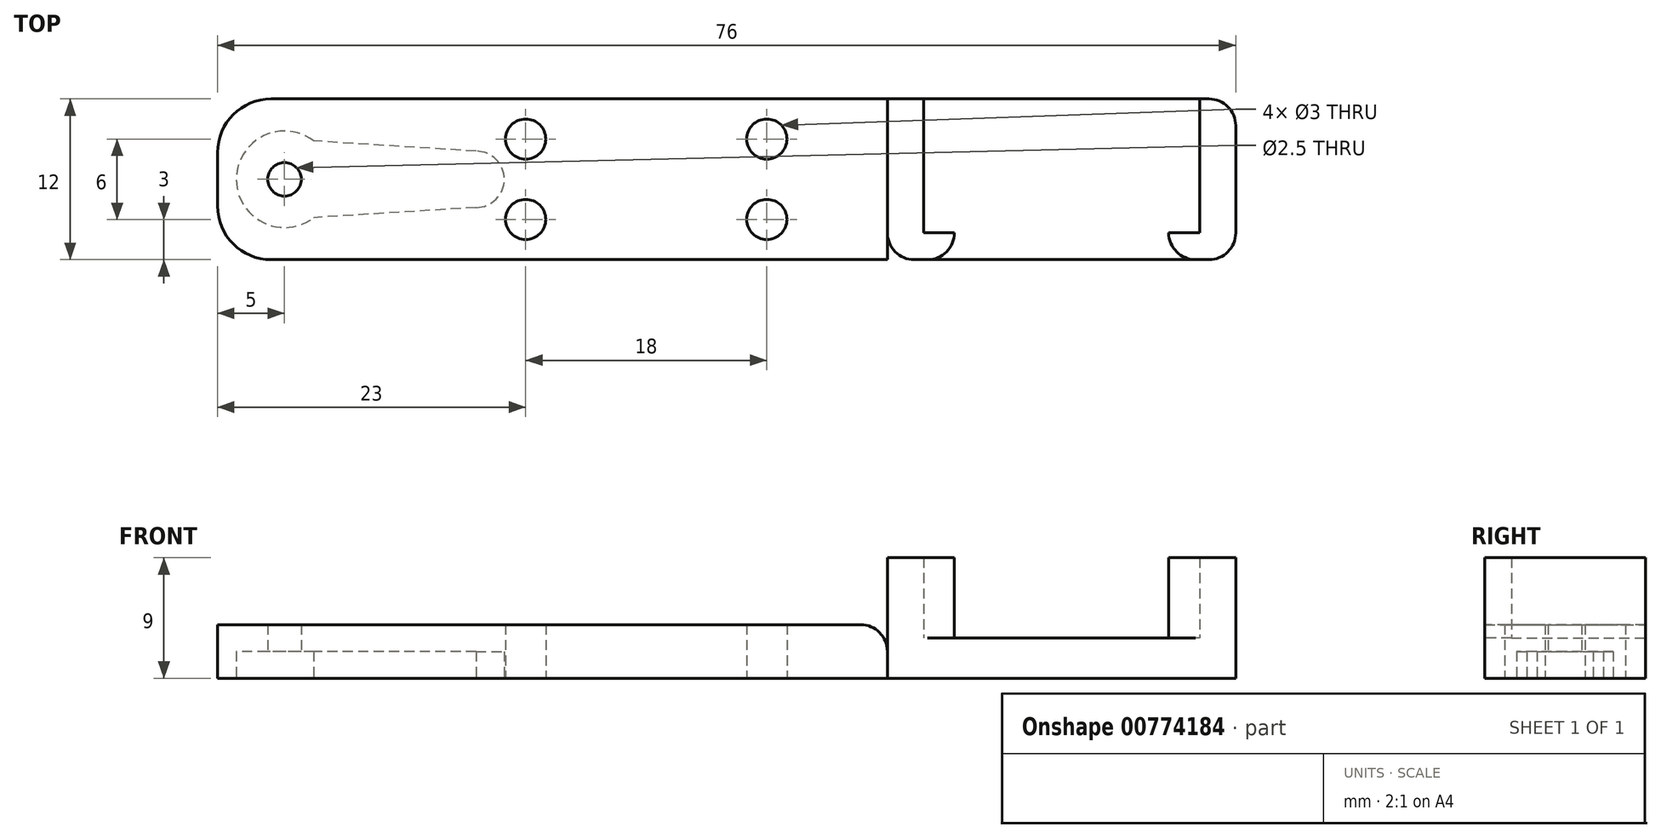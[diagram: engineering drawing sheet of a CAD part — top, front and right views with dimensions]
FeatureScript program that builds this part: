
annotation { "Feature Type Name" : "Feature", "Feature Type Description" : "" }
export const myFeature = defineFeature(function(context is Context, id is Id, definition is map)
    precondition{}
    {
        {
            var Q0;
            Q0=qCreatedBy(makeId("Top.planeOp"),FACE);
            var sketch = newSketch(context, id + "F0", { "sketchPlane" : qUnion([Q0])});
            skCircle(sketch, "E0", {"center": v(0, 0) * mm, "radius": 3.6 * mm});
            skLineSegment(sketch, "E1", {"start": v(0, 0) * mm, "end": v(0, 3) * mm});
            skLineSegment(sketch, "E2", {"start": v(0, 0) * mm, "end": v(0, -3) * mm, "construction": true});
            skLineSegment(sketch, "E3", {"start": v(0, 0) * mm, "end": v(14.3, 0) * mm});
            skLineSegment(sketch, "E4", {"start": v(14.3, 0) * mm, "end": v(14.3, -2.1) * mm});
            skArc(sketch, "E5", {"start": v(14.3, -2.1) * mm, "mid": v(16.4, 0) * mm, "end": v(14.3, 2.1) * mm});
            skLineSegment(sketch, "E6", {"start": v(14.3, 2.1) * mm, "end": v(0, 3) * mm});
            skLineSegment(sketch, "E7", {"start": v(14.3, -2.1) * mm, "end": v(0, -3) * mm});
            skSolve(sketch);
        }
        {
            var Q0;
            Q0 = qSketchRegion(id + "F0", true);
            extrude(context, id + "F1", {"entities" : qUnion([Q0]), "depth" : 2 * mm, "offsetDistance" : 25 * mm});
        }
        {
            var Q0;
            Q0=qCreatedBy(makeId("Top.planeOp"),FACE);
            var sketch = newSketch(context, id + "F2", { "sketchPlane" : qUnion([Q0])});
            skLineSegment(sketch, "E8.bottom", {"start": v(25, -6) * mm, "end": v(-25, -6) * mm});
            skLineSegment(sketch, "E8.top", {"start": v(25, 6) * mm, "end": v(-25, 6) * mm});
            skLineSegment(sketch, "E8.left", {"start": v(25, -6) * mm, "end": v(25, 6) * mm});
            skLineSegment(sketch, "E8.right", {"start": v(-25, -6) * mm, "end": v(-25, 6) * mm});
            skPoint(sketch, "E8.middle", {"position": v(0, 0) * mm});
            skSolve(sketch);
        }
        {
            var Q0;
            Q0 = qSketchRegion(id + "F2", true);
            extrude(context, id + "F3", {"entities" : qUnion([Q0]), "depth" : 4 * mm, "offsetDistance" : 25 * mm});
        }
        {
            var Q0;
            Q0=makeQuery(id+"F3.opExtrude","SWEPT_BODY",BODY,{"disambiguationData":[OSD([sQuery(id+"F2.wireOp",EDGE,"E8.bottom"),sQuery(id+"F2.wireOp",EDGE,"E8.top"),sQuery(id+"F2.wireOp",EDGE,"E8.left"),sQuery(id+"F2.wireOp",EDGE,"E8.right")])]});
            transform(context, id + "F4", {"entities" : qUnion([Q0]), "transformType" : TransformType.TRANSLATION_3D, "dx" : 20 * mm, "dy" : 0 * mm, "dz" : 0 * mm, "makeCopy" : false});
        }
        {
            var Q0;
            Q0=makeQuery(id+"F1.opExtrude","SWEPT_BODY",BODY,{"disambiguationData":[OSD([sQuery(id+"F0.wireOp",EDGE,"E0"),sQuery(id+"F0.wireOp",EDGE,"GIS3N8ls-1sfF-PQuO-XVTb-pW0GfDq8woWl"),sQuery(id+"F0.wireOp",EDGE,"lqkoCDOD-IdBk-z7gv-XOQQ-z2TdwHDsr1bX"),sQuery(id+"F0.wireOp",EDGE,"BW24nIRw-3JA8-FJTp-dAX4-ofwnhSPErRwU")])]});
            var Q1;
            Q1=makeQuery(id+"F3.opExtrude","SWEPT_BODY",BODY,{"disambiguationData":[OSD([sQuery(id+"F2.wireOp",EDGE,"E8.bottom"),sQuery(id+"F2.wireOp",EDGE,"E8.top"),sQuery(id+"F2.wireOp",EDGE,"E8.left"),sQuery(id+"F2.wireOp",EDGE,"E8.right")])]});
            booleanBodies(context, id + "F5", {"operationType" : BooleanOperationType.SUBTRACTION, "tools" : qUnion([Q0]), "targets" : qUnion([Q1])});
        }
        {
            var Q0;
            Q0=qCreatedBy(makeId("Top.planeOp"),FACE);
            var sketch = newSketch(context, id + "F6", { "sketchPlane" : qUnion([Q0])});
            skLineSegment(sketch, "E9", {"start": v(0, 0) * mm, "end": v(45, 0) * mm});
            skLineSegment(sketch, "E10", {"start": v(45, 0) * mm, "end": v(45, 6) * mm});
            skLineSegment(sketch, "E11", {"start": v(45, 6) * mm, "end": v(71, 6) * mm});
            skLineSegment(sketch, "E12", {"start": v(71, 6) * mm, "end": v(71, -6) * mm});
            skLineSegment(sketch, "E13", {"start": v(71, -6) * mm, "end": v(45, -6) * mm});
            skLineSegment(sketch, "E14", {"start": v(45, -6) * mm, "end": v(45, 0) * mm});
            skSolve(sketch);
        }
        {
            var Q0;
            Q0=makeQuery(id+"F3.opExtrude","SWEPT_EDGE",EDGE,{"disambiguationData":[OSD([sQuery(id+"F2.wireOp",EDGE,"E8.bottom"),sQuery(id+"F2.wireOp",EDGE,"E8.right")])]});
            var Q1;
            Q1=makeQuery(id+"F3.opExtrude","SWEPT_EDGE",EDGE,{"disambiguationData":[OSD([sQuery(id+"F2.wireOp",EDGE,"E8.top"),sQuery(id+"F2.wireOp",EDGE,"E8.right")])]});
            fillet(context, id + "F7", {"entities" : qUnion([Q0, Q1]), "radius" : 4 * mm, "tangentPropagation" : true, "allowEdgeOverflow" : false});
        }
        {
            var Q0;
            Q0 = qSketchRegion(id + "F6", true);
            extrude(context, id + "F8", {"entities" : qUnion([Q0]), "depth" : 9 * mm, "offsetDistance" : 25 * mm});
        }
        {
            var Q0;
            Q0=qCreatedBy(makeId("Top.planeOp"),FACE);
            var sketch = newSketch(context, id + "F9", { "sketchPlane" : qUnion([Q0])});
            skLineSegment(sketch, "E15", {"start": v(0, 0) * mm, "end": v(58, 0) * mm});
            skPoint(sketch, "E16.middle", {"position": v(58, 0) * mm});
            skLineSegment(sketch, "E17.bottom", {"start": v(68.3, -5) * mm, "end": v(47.7, -5) * mm});
            skLineSegment(sketch, "E17.top", {"start": v(68.3, 5) * mm, "end": v(47.7, 5) * mm});
            skLineSegment(sketch, "E17.left", {"start": v(68.3, -5) * mm, "end": v(68.3, 5) * mm});
            skLineSegment(sketch, "E17.right", {"start": v(47.7, -5) * mm, "end": v(47.7, 5) * mm});
            skLineSegment(sketch, "E18", {"start": v(58, -5) * mm, "end": v(50, -5) * mm});
            skLineSegment(sketch, "E19", {"start": v(50, -5) * mm, "end": v(50, -10) * mm});
            skLineSegment(sketch, "E20", {"start": v(50, -10) * mm, "end": v(66, -10) * mm});
            skLineSegment(sketch, "E21", {"start": v(66, -10) * mm, "end": v(66, -5) * mm});
            skSolve(sketch);
        }
        {
            var Q0;
            Q0 = qSketchRegion(id + "F9", true);
            extrude(context, id + "F10", {"entities" : qUnion([Q0]), "depth" : 16 * mm, "offsetDistance" : 25 * mm});
        }
        {
            var Q0;
            Q0=makeQuery(id+"F10.opExtrude","SWEPT_BODY",BODY,{"disambiguationData":[OSD([sQuery(id+"F9.wireOp",EDGE,"E17.bottom"),sQuery(id+"F9.wireOp",EDGE,"E17.top"),sQuery(id+"F9.wireOp",EDGE,"E17.left"),sQuery(id+"F9.wireOp",EDGE,"E17.right"),sQuery(id+"F9.wireOp",EDGE,"E19"),sQuery(id+"F9.wireOp",EDGE,"E20"),sQuery(id+"F9.wireOp",EDGE,"E21")])]});
            transform(context, id + "F11", {"entities" : qUnion([Q0]), "transformType" : TransformType.TRANSLATION_3D, "dx" : 0 * mm, "dy" : 1 * mm, "dz" : 3 * mm, "makeCopy" : false});
        }
        {
            var Q0;
            Q0=makeQuery(id+"F10.opExtrude","SWEPT_BODY",BODY,{"disambiguationData":[OSD([sQuery(id+"F9.wireOp",EDGE,"E17.bottom"),sQuery(id+"F9.wireOp",EDGE,"E17.top"),sQuery(id+"F9.wireOp",EDGE,"E17.left"),sQuery(id+"F9.wireOp",EDGE,"E17.right"),sQuery(id+"F9.wireOp",EDGE,"E19"),sQuery(id+"F9.wireOp",EDGE,"E20"),sQuery(id+"F9.wireOp",EDGE,"E21")])]});
            var Q1;
            Q1=makeQuery(id+"F8.opExtrude","SWEPT_BODY",BODY,{"disambiguationData":[OSD([sQuery(id+"F6.wireOp",EDGE,"E10"),sQuery(id+"F6.wireOp",EDGE,"E11"),sQuery(id+"F6.wireOp",EDGE,"E12"),sQuery(id+"F6.wireOp",EDGE,"E13"),sQuery(id+"F6.wireOp",EDGE,"E14")])]});
            booleanBodies(context, id + "F12", {"operationType" : BooleanOperationType.SUBTRACTION, "tools" : qUnion([Q0]), "targets" : qUnion([Q1])});
        }
        {
            var Q0;
            Q0=qCreatedBy(makeId("Top.planeOp"),FACE);
            var sketch = newSketch(context, id + "F13", { "sketchPlane" : qUnion([Q0])});
            skCircle(sketch, "E22", {"center": v(0, 0) * mm, "radius": 1.25 * mm});
            skSolve(sketch);
        }
        {
            var Q0;
            Q0 = qSketchRegion(id + "F13", true);
            extrude(context, id + "F14", {"entities" : qUnion([Q0]), "depth" : 25 * mm, "offsetDistance" : 25 * mm});
        }
        {
            var Q0;
            Q0=makeQuery(id+"F14.opExtrude","SWEPT_BODY",BODY,{"disambiguationData":[OSD([sQuery(id+"F13.wireOp",EDGE,"E22")])]});
            var Q1;
            Q1=makeQuery(id+"F3.opExtrude","SWEPT_BODY",BODY,{"disambiguationData":[OSD([sQuery(id+"F2.wireOp",EDGE,"E8.bottom"),sQuery(id+"F2.wireOp",EDGE,"E8.top"),sQuery(id+"F2.wireOp",EDGE,"E8.left"),sQuery(id+"F2.wireOp",EDGE,"E8.right")])]});
            booleanBodies(context, id + "F15", {"operationType" : BooleanOperationType.SUBTRACTION, "tools" : qUnion([Q0]), "targets" : qUnion([Q1])});
        }
        {
            var Q0;
            Q0=qCreatedBy(makeId("Top.planeOp"),FACE);
            var sketch = newSketch(context, id + "F16", { "sketchPlane" : qUnion([Q0])});
            skLineSegment(sketch, "E23", {"start": v(0, 0) * mm, "end": v(18, 0) * mm});
            skLineSegment(sketch, "E24", {"start": v(18, 0) * mm, "end": v(36, 0) * mm});
            skLineSegment(sketch, "E25", {"start": v(36, 0) * mm, "end": v(36, -3) * mm});
            skLineSegment(sketch, "E26", {"start": v(18, 0) * mm, "end": v(18, -3) * mm});
            skLineSegment(sketch, "E27", {"start": v(18, 0) * mm, "end": v(18, 3) * mm});
            skLineSegment(sketch, "E28", {"start": v(36, 0) * mm, "end": v(36, 3) * mm});
            skCircle(sketch, "E29", {"center": v(18, -3) * mm, "radius": 1.5 * mm});
            skCircle(sketch, "E30", {"center": v(18, 3) * mm, "radius": 1.5 * mm});
            skCircle(sketch, "E31", {"center": v(36, -3) * mm, "radius": 1.5 * mm});
            skCircle(sketch, "E32", {"center": v(36, 3) * mm, "radius": 1.5 * mm});
            skSolve(sketch);
        }
        {
            var Q0;
            Q0 = qSketchRegion(id + "F16", true);
            extrude(context, id + "F17", {"entities" : qUnion([Q0]), "depth" : 25 * mm, "offsetDistance" : 25 * mm});
        }
        {
            var Q0;
            Q0=makeQuery(id+"F17.opExtrude","SWEPT_BODY",BODY,{"disambiguationData":[OSD([sQuery(id+"F16.wireOp",EDGE,"E29")])]});
            var Q1;
            Q1=makeQuery(id+"F17.opExtrude","SWEPT_BODY",BODY,{"disambiguationData":[OSD([sQuery(id+"F16.wireOp",EDGE,"E30")])]});
            var Q2;
            Q2=makeQuery(id+"F17.opExtrude","SWEPT_BODY",BODY,{"disambiguationData":[OSD([sQuery(id+"F16.wireOp",EDGE,"E32")])]});
            var Q3;
            Q3=makeQuery(id+"F17.opExtrude","SWEPT_BODY",BODY,{"disambiguationData":[OSD([sQuery(id+"F16.wireOp",EDGE,"E31")])]});
            var Q4;
            Q4=makeQuery(id+"F3.opExtrude","SWEPT_BODY",BODY,{"disambiguationData":[OSD([sQuery(id+"F2.wireOp",EDGE,"E8.bottom"),sQuery(id+"F2.wireOp",EDGE,"E8.top"),sQuery(id+"F2.wireOp",EDGE,"E8.left"),sQuery(id+"F2.wireOp",EDGE,"E8.right")])]});
            booleanBodies(context, id + "F18", {"operationType" : BooleanOperationType.SUBTRACTION, "tools" : qUnion([Q0, Q1, Q2, Q3]), "targets" : qUnion([Q4])});
        }
        {
            var Q0;
            Q0=makeQuery(id+"F8.opExtrude","SWEPT_EDGE",EDGE,{"disambiguationData":[OSD([sQuery(id+"F6.wireOp",EDGE,"E12"),sQuery(id+"F6.wireOp",EDGE,"E13")])]});
            var Q1;
            Q1=makeQuery(id+"F8.opExtrude","SWEPT_EDGE",EDGE,{"disambiguationData":[OSD([sQuery(id+"F6.wireOp",EDGE,"E11"),sQuery(id+"F6.wireOp",EDGE,"E12")])]});
            var Q2;
            Q2=makeQuery(id+"F3.opExtrude","CAP_EDGE",EDGE,{"disambiguationData":[OSD([sQuery(id+"F2.wireOp",EDGE,"E8.left")])],"isStart":false});
            var Q3;
            Q3=makeQuery(id+"F8.opExtrude","SWEPT_EDGE",EDGE,{"disambiguationData":[OSD([sQuery(id+"F6.wireOp",EDGE,"E13"),sQuery(id+"F6.wireOp",EDGE,"E14")])]});
            var Q4;
            Q4=makeQuery(id+"F12.opBoolean","INTERSECT",EDGE,{"derivedFrom":[makeQuery(id+"F8.opExtrude","SWEPT_FACE",FACE,{"disambiguationData":[OSD([sQuery(id+"F6.wireOp",EDGE,"E13")])]}),makeQuery(id+"F10.opExtrude","SWEPT_FACE",FACE,{"disambiguationData":[OSD([sQuery(id+"F9.wireOp",EDGE,"E21")])]})]});
            var Q5;
            Q5=makeQuery(id+"F12.opBoolean","INTERSECT",EDGE,{"derivedFrom":[makeQuery(id+"F8.opExtrude","SWEPT_FACE",FACE,{"disambiguationData":[OSD([sQuery(id+"F6.wireOp",EDGE,"E13")])]}),makeQuery(id+"F10.opExtrude","SWEPT_FACE",FACE,{"disambiguationData":[OSD([sQuery(id+"F9.wireOp",EDGE,"E19")])]})]});
            fillet(context, id + "F19", {"entities" : qUnion([Q0, Q1, Q2, Q3, Q4, Q5]), "radius" : 2 * mm, "tangentPropagation" : true, "allowEdgeOverflow" : false});
        }
    });
